# Revit family: NXAC_Series
name_source: partatom
category: Electrical Equipment
units: mm (PartAtom-declared; Revit-internal decimal feet)

## family parameters
Cut with Voids When Loaded = No
Host = Face
OmniClass Number = 23.80.30.11.17
OmniClass Title = Distribution Boards and Control Panels
Part Type = Equipment Switch
Room Calculation Point = No
Round Connector Dimension = Use Diameter
Shared = No

## types (1)
- NXAC
    Apparent Load = 0.000 VA
    Assembly Code = D50
    Certifications = UL916, UL924 and cUL
    Connector Description 1 = Power Supply
    Connector Description 2 = Controls
    Construction = NEMA1 metal enclosure
    Default Elevation = 48 "
    Description = NX Area Controller
    Device Material = Gray
    Frequency = 60 Hz
    Load Classification = Power
    Manufacturer = NX Lighting Controls
    Model = NXAC Series
    Operating Temperature = 0°C to 40°C (32°F to 104°F)
    Power Factor = 1
    Relative Humidity = 0 to 95%
    Type Comments = Electrical Equipment
    URL = https://www.currentlighting.com
    Voltage = 120V
    Warranty = Five-year limited
    Weight = 8 kg
    zz Length 1 = 13.5 "
    zz Length 2 = 14.51 "
    zz Length 3 = 4.08 "

## geometry (parser evidence)
native form markers: Sweep x2
no freeform markers — native parametric forms only
